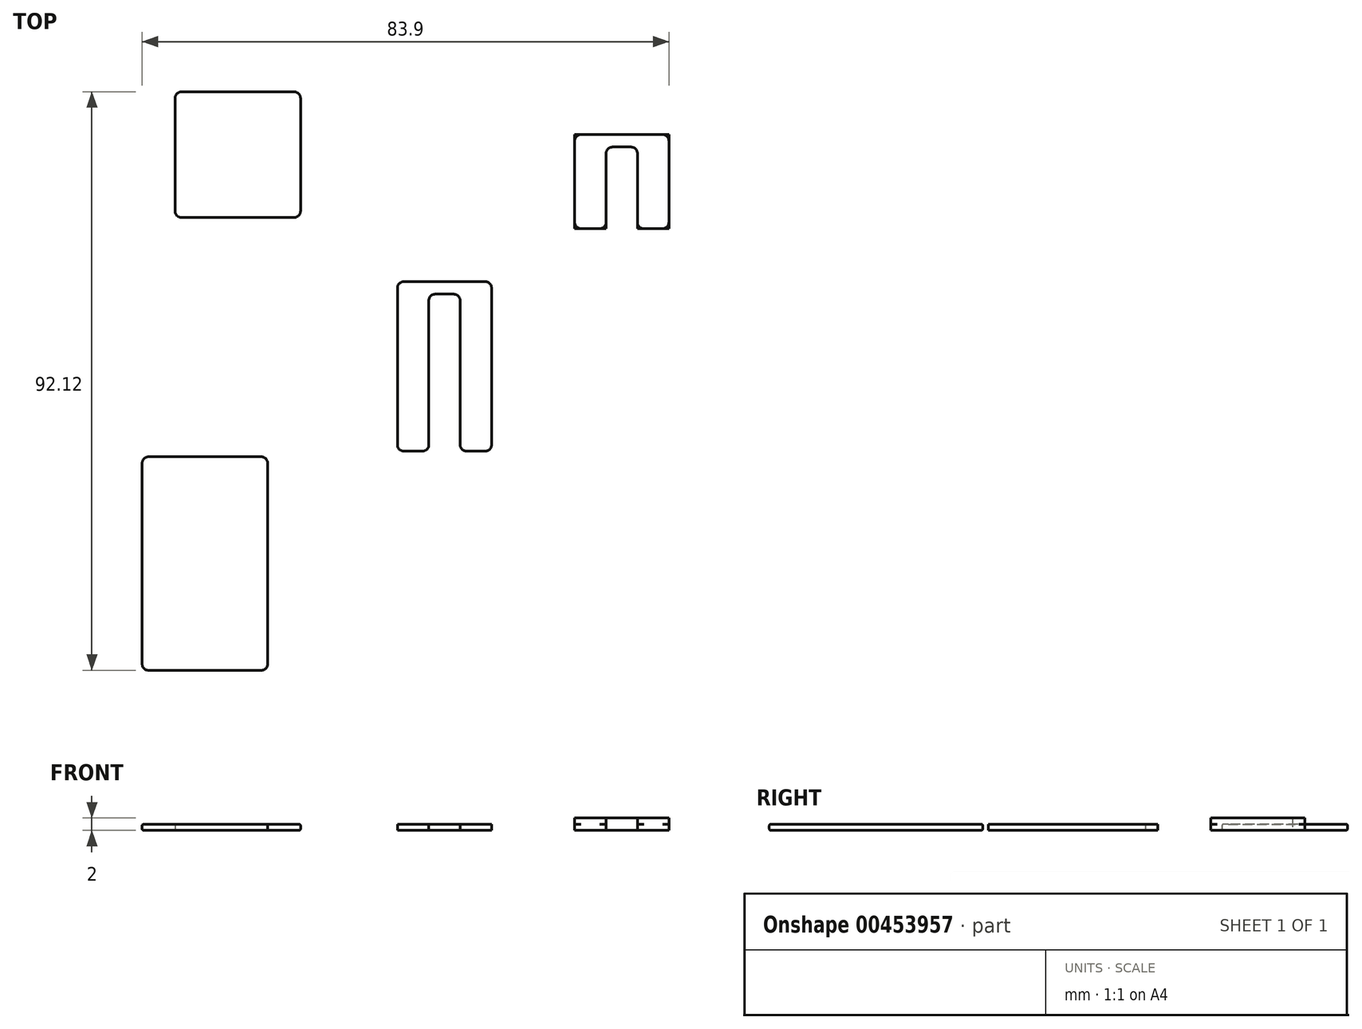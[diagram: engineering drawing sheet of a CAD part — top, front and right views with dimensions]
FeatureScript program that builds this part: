
annotation { "Feature Type Name" : "Feature", "Feature Type Description" : "" }
export const myFeature = defineFeature(function(context is Context, id is Id, definition is map)
    precondition{}
    {
        {
            var Q0;
            Q0=qCreatedBy(makeId("Top.planeOp"),FACE);
            var sketch = newSketch(context, id + "F0", { "sketchPlane" : qUnion([Q0])});
            skLineSegment(sketch, "E0", {"start": v(-42.93, 50.22) * mm, "end": v(-42.93, 30.22) * mm});
            skLineSegment(sketch, "E1", {"start": v(-42.93, 30.22) * mm, "end": v(-22.93, 30.22) * mm});
            skLineSegment(sketch, "E2", {"start": v(-22.93, 30.22) * mm, "end": v(-22.93, 50.22) * mm});
            skLineSegment(sketch, "E3", {"start": v(-22.93, 50.22) * mm, "end": v(-42.93, 50.22) * mm});
            skPoint(sketch, "E4.start.orphan", {"position": v(5.22, 50.22) * mm});
            skSolve(sketch);
        }
        {
            var Q0;
            Q0=makeQuery(id+"F0.imprint","IMPRINT",FACE,{"disambiguationData":[TD([[makeQuery(id+"F0.imprint","IMPRINT",EDGE,{"derivedFrom":sQuery(id+"F0.wireOp",EDGE,"E0")}),1.0]])]});
            extrude(context, id + "F1", {"entities" : qUnion([Q0]), "depth" : 1 * mm});
        }
        {
            var Q0;
            Q0=makeQuery(id+"F1.opExtrude","SWEPT_EDGE",EDGE,{"disambiguationData":[OSD([sQuery(id+"F0.wireOp",EDGE,"E0"),sQuery(id+"F0.wireOp",EDGE,"E3")])]});
            var Q1;
            Q1=makeQuery(id+"F1.opExtrude","SWEPT_EDGE",EDGE,{"disambiguationData":[OSD([sQuery(id+"F0.wireOp",EDGE,"E2"),sQuery(id+"F0.wireOp",EDGE,"E3")])]});
            var Q2;
            Q2=makeQuery(id+"F1.opExtrude","SWEPT_EDGE",EDGE,{"disambiguationData":[OSD([sQuery(id+"F0.wireOp",EDGE,"E1"),sQuery(id+"F0.wireOp",EDGE,"E2")])]});
            var Q3;
            Q3=makeQuery(id+"F1.opExtrude","SWEPT_EDGE",EDGE,{"disambiguationData":[OSD([sQuery(id+"F0.wireOp",EDGE,"E0"),sQuery(id+"F0.wireOp",EDGE,"E1")])]});
            fillet(context, id + "F2", {"entities" : qUnion([Q0, Q1, Q2, Q3]), "radius" : 1 * mm, "tangentPropagation" : true, "allowEdgeOverflow" : false});
        }
        {
            var Q0;
            Q0=makeQuery(id+"F1.opExtrude","CAP_EDGE",EDGE,{"disambiguationData":[OSD([sQuery(id+"F0.wireOp",EDGE,"E1")])],"isStart":false});
            var Q1;
            Q1=makeQuery(id+"F1.opExtrude","SWEPT_FACE",FACE,{"disambiguationData":[OSD([sQuery(id+"F0.wireOp",EDGE,"E2")])]});
            fillet(context, id + "F3", {"entities" : qUnion([Q0, Q1]), "radius" : .25 * mm, "tangentPropagation" : true, "allowEdgeOverflow" : false});
        }
        {
            var Q0;
            Q0=qCreatedBy(makeId("Top.planeOp"),FACE);
            var sketch = newSketch(context, id + "F4", { "sketchPlane" : qUnion([Q0])});
            skLineSegment(sketch, "E5", {"start": v(20.74, 43.43) * mm, "end": v(35.74, 43.43) * mm});
            skLineSegment(sketch, "E6", {"start": v(35.74, 43.43) * mm, "end": v(35.74, 28.43) * mm});
            skLineSegment(sketch, "E7", {"start": v(35.74, 28.43) * mm, "end": v(30.74, 28.43) * mm});
            skLineSegment(sketch, "E8", {"start": v(30.74, 28.43) * mm, "end": v(30.74, 41.43) * mm});
            skLineSegment(sketch, "E9", {"start": v(25.74, 41.43) * mm, "end": v(25.74, 28.43) * mm});
            skLineSegment(sketch, "E10", {"start": v(20.74, 28.43) * mm, "end": v(20.74, 43.43) * mm});
            skLineSegment(sketch, "E11", {"start": v(20.74, 28.43) * mm, "end": v(25.74, 28.43) * mm});
            skLineSegment(sketch, "E12", {"start": v(25.74, 41.43) * mm, "end": v(30.74, 41.43) * mm});
            skLineSegment(sketch, "E13", {"start": v(-7.5, 20) * mm, "end": v(7.5, 20) * mm});
            skLineSegment(sketch, "E14", {"start": v(7.5, 20) * mm, "end": v(7.5, -7) * mm});
            skLineSegment(sketch, "E15", {"start": v(-7.5, -7) * mm, "end": v(-7.5, 20) * mm});
            skLineSegment(sketch, "E16", {"start": v(-7.5, -7) * mm, "end": v(-2.5, -7) * mm});
            skLineSegment(sketch, "E17", {"start": v(7.5, -7) * mm, "end": v(2.5, -7) * mm});
            skLineSegment(sketch, "E18", {"start": v(-2.5, -7) * mm, "end": v(-2.5, 18) * mm});
            skLineSegment(sketch, "E19", {"start": v(2.5, -7) * mm, "end": v(2.5, 18) * mm});
            skLineSegment(sketch, "E20", {"start": v(-2.5, 18) * mm, "end": v(2.5, 18) * mm});
            skSolve(sketch);
        }
        {
            var Q0;
            Q0=makeQuery(id+"F4.imprint","IMPRINT",FACE,{"disambiguationData":[TD([[makeQuery(id+"F4.imprint","IMPRINT",EDGE,{"derivedFrom":sQuery(id+"F4.wireOp",EDGE,"E5")}),-1.0]])]});
            extrude(context, id + "F5", {"entities" : qUnion([Q0]), "depth" : 2 * mm});
        }
        {
            var Q0;
            Q0=makeQuery(id+"F5.opExtrude","SWEPT_EDGE",EDGE,{"disambiguationData":[OSD([sQuery(id+"F4.wireOp",EDGE,"E5"),sQuery(id+"F4.wireOp",EDGE,"E6")])]});
            var Q1;
            Q1=makeQuery(id+"F5.opExtrude","SWEPT_EDGE",EDGE,{"disambiguationData":[OSD([sQuery(id+"F4.wireOp",EDGE,"E5"),sQuery(id+"F4.wireOp",EDGE,"E10")])]});
            var Q2;
            Q2=makeQuery(id+"F5.opExtrude","SWEPT_EDGE",EDGE,{"disambiguationData":[OSD([sQuery(id+"F4.wireOp",EDGE,"E6"),sQuery(id+"F4.wireOp",EDGE,"E7")])]});
            var Q3;
            Q3=makeQuery(id+"F5.opExtrude","SWEPT_EDGE",EDGE,{"disambiguationData":[OSD([sQuery(id+"F4.wireOp",EDGE,"E7"),sQuery(id+"F4.wireOp",EDGE,"E8")])]});
            var Q4;
            Q4=makeQuery(id+"F5.opExtrude","SWEPT_EDGE",EDGE,{"disambiguationData":[OSD([sQuery(id+"F4.wireOp",EDGE,"E9"),sQuery(id+"F4.wireOp",EDGE,"E11")])]});
            var Q5;
            Q5=makeQuery(id+"F5.opExtrude","SWEPT_EDGE",EDGE,{"disambiguationData":[OSD([sQuery(id+"F4.wireOp",EDGE,"E10"),sQuery(id+"F4.wireOp",EDGE,"E11")])]});
            var Q6;
            Q6=makeQuery(id+"F5.opExtrude","SWEPT_EDGE",EDGE,{"disambiguationData":[OSD([sQuery(id+"F4.wireOp",EDGE,"qiDKm8Bc-0KG6-eblP-MNoN-9GVUghN3DcYW"),sQuery(id+"F4.wireOp",EDGE,"E9")])]});
            fillet(context, id + "F6", {"entities" : qUnion([Q0, Q1, Q2, Q3, Q4, Q5, Q6]), "radius" : 1 * mm, "tangentPropagation" : true, "allowEdgeOverflow" : false});
        }
        {
            var Q0;
            Q0=makeQuery(id+"F5.opExtrude","SWEPT_EDGE",EDGE,{"disambiguationData":[OSD([sQuery(id+"F4.wireOp",EDGE,"E8"),sQuery(id+"F4.wireOp",EDGE,"qiDKm8Bc-0KG6-eblP-MNoN-9GVUghN3DcYW")])]});
            fillet(context, id + "F7", {"entities" : qUnion([Q0]), "radius" : 1 * mm, "tangentPropagation" : true, "allowEdgeOverflow" : false});
        }
        {
            var Q0;
            Q0 = qSketchRegion(id + "F4", true);
            extrude(context, id + "F8", {"entities" : qUnion([Q0]), "operationType" : NewBodyOperationType.ADD, "depth" : 1 * mm});
        }
        {
            var Q0;
            Q0=makeQuery(id+"F8.opExtrude","SWEPT_EDGE",EDGE,{"disambiguationData":[OSD([sQuery(id+"F4.wireOp",EDGE,"E15"),sQuery(id+"F4.wireOp",EDGE,"E16")])]});
            var Q1;
            Q1=makeQuery(id+"F8.opExtrude","SWEPT_EDGE",EDGE,{"disambiguationData":[OSD([sQuery(id+"F4.wireOp",EDGE,"E17"),sQuery(id+"F4.wireOp",EDGE,"E19")])]});
            var Q2;
            Q2=makeQuery(id+"F8.opExtrude","SWEPT_EDGE",EDGE,{"disambiguationData":[OSD([sQuery(id+"F4.wireOp",EDGE,"E16"),sQuery(id+"F4.wireOp",EDGE,"E18")])]});
            var Q3;
            Q3=makeQuery(id+"F8.opExtrude","SWEPT_EDGE",EDGE,{"disambiguationData":[OSD([sQuery(id+"F4.wireOp",EDGE,"E14"),sQuery(id+"F4.wireOp",EDGE,"E17")])]});
            var Q4;
            Q4=makeQuery(id+"F8.opExtrude","SWEPT_EDGE",EDGE,{"disambiguationData":[OSD([sQuery(id+"F4.wireOp",EDGE,"E13"),sQuery(id+"F4.wireOp",EDGE,"E14")])]});
            var Q5;
            Q5=makeQuery(id+"F8.opExtrude","SWEPT_EDGE",EDGE,{"disambiguationData":[OSD([sQuery(id+"F4.wireOp",EDGE,"E13"),sQuery(id+"F4.wireOp",EDGE,"E15")])]});
            fillet(context, id + "F9", {"entities" : qUnion([Q0, Q1, Q2, Q3, Q4, Q5]), "radius" : 1 * mm, "tangentPropagation" : true, "allowEdgeOverflow" : false});
        }
        {
            var Q0;
            Q0=qCreatedBy(makeId("Top.planeOp"),FACE);
            var sketch = newSketch(context, id + "F10", { "sketchPlane" : qUnion([Q0])});
            skLineSegment(sketch, "E21", {"start": v(-48.16, -7.9) * mm, "end": v(-48.16, -41.9) * mm});
            skLineSegment(sketch, "E22", {"start": v(-48.16, -41.9) * mm, "end": v(-28.16, -41.9) * mm});
            skLineSegment(sketch, "E23", {"start": v(-28.16, -41.9) * mm, "end": v(-28.16, -7.9) * mm});
            skLineSegment(sketch, "E24", {"start": v(-28.16, -7.9) * mm, "end": v(-48.16, -7.9) * mm});
            skSolve(sketch);
        }
        {
            var Q0;
            Q0=makeQuery(id+"F10.imprint","IMPRINT",FACE,{"disambiguationData":[TD([[makeQuery(id+"F10.imprint","IMPRINT",EDGE,{"derivedFrom":sQuery(id+"F10.wireOp",EDGE,"E21")}),1.0]])]});
            extrude(context, id + "F11", {"entities" : qUnion([Q0]), "depth" : 1 * mm});
        }
        {
            var Q0;
            Q0=makeQuery(id+"F11.opExtrude","SWEPT_EDGE",EDGE,{"disambiguationData":[OSD([sQuery(id+"F10.wireOp",EDGE,"E22"),sQuery(id+"F10.wireOp",EDGE,"E23")])]});
            var Q1;
            Q1=makeQuery(id+"F11.opExtrude","SWEPT_EDGE",EDGE,{"disambiguationData":[OSD([sQuery(id+"F10.wireOp",EDGE,"E23"),sQuery(id+"F10.wireOp",EDGE,"E24")])]});
            var Q2;
            Q2=makeQuery(id+"F11.opExtrude","SWEPT_EDGE",EDGE,{"disambiguationData":[OSD([sQuery(id+"F10.wireOp",EDGE,"E21"),sQuery(id+"F10.wireOp",EDGE,"E22")])]});
            var Q3;
            Q3=makeQuery(id+"F11.opExtrude","SWEPT_EDGE",EDGE,{"disambiguationData":[OSD([sQuery(id+"F10.wireOp",EDGE,"E21"),sQuery(id+"F10.wireOp",EDGE,"E24")])]});
            fillet(context, id + "F12", {"entities" : qUnion([Q0, Q1, Q2, Q3]), "radius" : 1 * mm, "tangentPropagation" : true, "allowEdgeOverflow" : false});
        }
        {
            var Q0;
            Q0=makeQuery(id+"F11.opExtrude","CAP_FACE",FACE,{"disambiguationData":[OSD([sQuery(id+"F10.wireOp",EDGE,"E21"),sQuery(id+"F10.wireOp",EDGE,"E22"),sQuery(id+"F10.wireOp",EDGE,"E23"),sQuery(id+"F10.wireOp",EDGE,"E24")])],"isStart":false});
            var Q1;
            Q1=makeQuery(id+"F11.opExtrude","CAP_FACE",FACE,{"disambiguationData":[OSD([sQuery(id+"F10.wireOp",EDGE,"E21"),sQuery(id+"F10.wireOp",EDGE,"E22"),sQuery(id+"F10.wireOp",EDGE,"E23"),sQuery(id+"F10.wireOp",EDGE,"E24")])],"isStart":true});
            fillet(context, id + "F13", {"entities" : qUnion([Q0, Q1]), "radius" : .25 * mm, "tangentPropagation" : true, "allowEdgeOverflow" : false});
        }
        {
            var Q0;
            Q0=makeQuery(id+"F8.opExtrude","SWEPT_EDGE",EDGE,{"disambiguationData":[OSD([sQuery(id+"F4.wireOp",EDGE,"E18"),sQuery(id+"F4.wireOp",EDGE,"E20")])]});
            var Q1;
            Q1=makeQuery(id+"F8.opExtrude","SWEPT_EDGE",EDGE,{"disambiguationData":[OSD([sQuery(id+"F4.wireOp",EDGE,"E19"),sQuery(id+"F4.wireOp",EDGE,"E20")])]});
            fillet(context, id + "F14", {"entities" : qUnion([Q0, Q1]), "radius" : 1 * mm, "tangentPropagation" : true, "allowEdgeOverflow" : false});
        }
    });
